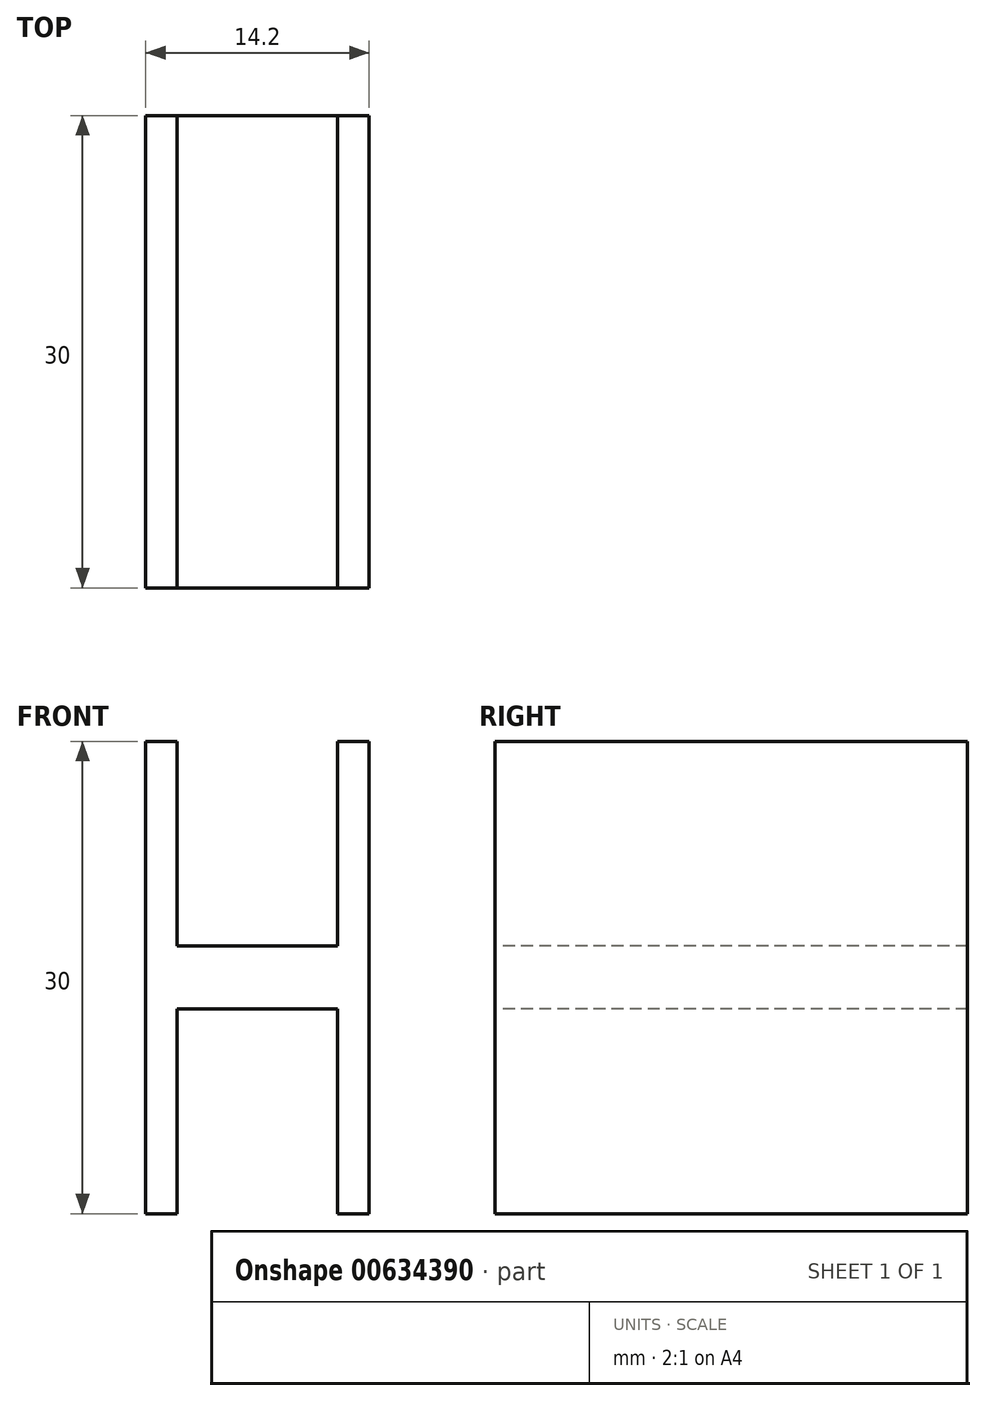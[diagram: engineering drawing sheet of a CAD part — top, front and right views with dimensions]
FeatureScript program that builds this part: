
annotation { "Feature Type Name" : "Feature", "Feature Type Description" : "" }
export const myFeature = defineFeature(function(context is Context, id is Id, definition is map)
    precondition{}
    {
        {
            var Q0;
            Q0=qCreatedBy(makeId("Front.planeOp"),FACE);
            var sketch = newSketch(context, id + "F0", { "sketchPlane" : qUnion([Q0])});
            skLineSegment(sketch, "E0", {"start": v(-15, 0) * mm, "end": v(15, 0) * mm});
            skLineSegment(sketch, "E1", {"start": v(15, 0) * mm, "end": v(15, 2) * mm});
            skLineSegment(sketch, "E2", {"start": v(15, 2) * mm, "end": v(7.1, 2) * mm});
            skLineSegment(sketch, "E3", {"start": v(7.1, 2) * mm, "end": v(7.1, 15) * mm});
            skLineSegment(sketch, "E4", {"start": v(7.1, 15) * mm, "end": v(5.1, 15) * mm});
            skLineSegment(sketch, "E5", {"start": v(5.1, 15) * mm, "end": v(5.1, 2) * mm});
            skLineSegment(sketch, "E6", {"start": v(5.1, 2) * mm, "end": v(-5.1, 2) * mm});
            skLineSegment(sketch, "E7", {"start": v(-5.1, 2) * mm, "end": v(-5.1, 15) * mm});
            skLineSegment(sketch, "E8", {"start": v(-5.1, 15) * mm, "end": v(-7.1, 15) * mm});
            skLineSegment(sketch, "E9", {"start": v(-7.1, 15) * mm, "end": v(-7.1, 2) * mm});
            skLineSegment(sketch, "E10", {"start": v(-7.1, 2) * mm, "end": v(-15, 2) * mm});
            skLineSegment(sketch, "E11", {"start": v(-15, 2) * mm, "end": v(-15, 0) * mm});
            skLineSegment(sketch, "E12", {"start": v(0, 0) * mm, "end": v(0, 2) * mm, "construction": true});
            skLineSegment(sketch, "E13", {"start": v(-7.1, 2) * mm, "end": v(-7.1, 0) * mm});
            skLineSegment(sketch, "E14", {"start": v(7.1, 2) * mm, "end": v(7.1, 0) * mm});
            skSolve(sketch);
        }
        {
            var Q0;
            Q0=makeQuery(id+"F0.imprint","IMPRINT",FACE,{"disambiguationData":[TD([[makeQuery(id+"F0.imprint","IMPRINT",EDGE,{"derivedFrom":sQuery(id+"F0.wireOp",EDGE,"E3")}),1.0]])]});
            extrude(context, id + "F1", {"entities" : qUnion([Q0]), "oppositeDirection" : true, "depth" : 30 * mm, "offsetDistance" : 25 * mm});
        }
        {
            var Q0;
            Q0=makeQuery(id+"F1.opExtrude","SWEPT_BODY",BODY,{"disambiguationData":[OSD([sQuery(id+"F0.wireOp",EDGE,"E0"),sQuery(id+"F0.wireOp",EDGE,"E3"),sQuery(id+"F0.wireOp",EDGE,"E4"),sQuery(id+"F0.wireOp",EDGE,"E5"),sQuery(id+"F0.wireOp",EDGE,"E6"),sQuery(id+"F0.wireOp",EDGE,"E7"),sQuery(id+"F0.wireOp",EDGE,"E8"),sQuery(id+"F0.wireOp",EDGE,"E9"),sQuery(id+"F0.wireOp",EDGE,"E13"),sQuery(id+"F0.wireOp",EDGE,"E14")])]});
            var Q1;
            Q1=makeQuery(id+"F1.opExtrude","SWEPT_FACE",FACE,{"disambiguationData":[OSD([sQuery(id+"F0.wireOp",EDGE,"E0")])]});
            mirror(context, id + "F2", {"operationType" : NewBodyOperationType.ADD, "entities" : qUnion([Q0]), "mirrorPlane" : qUnion([Q1])});
        }
    });
